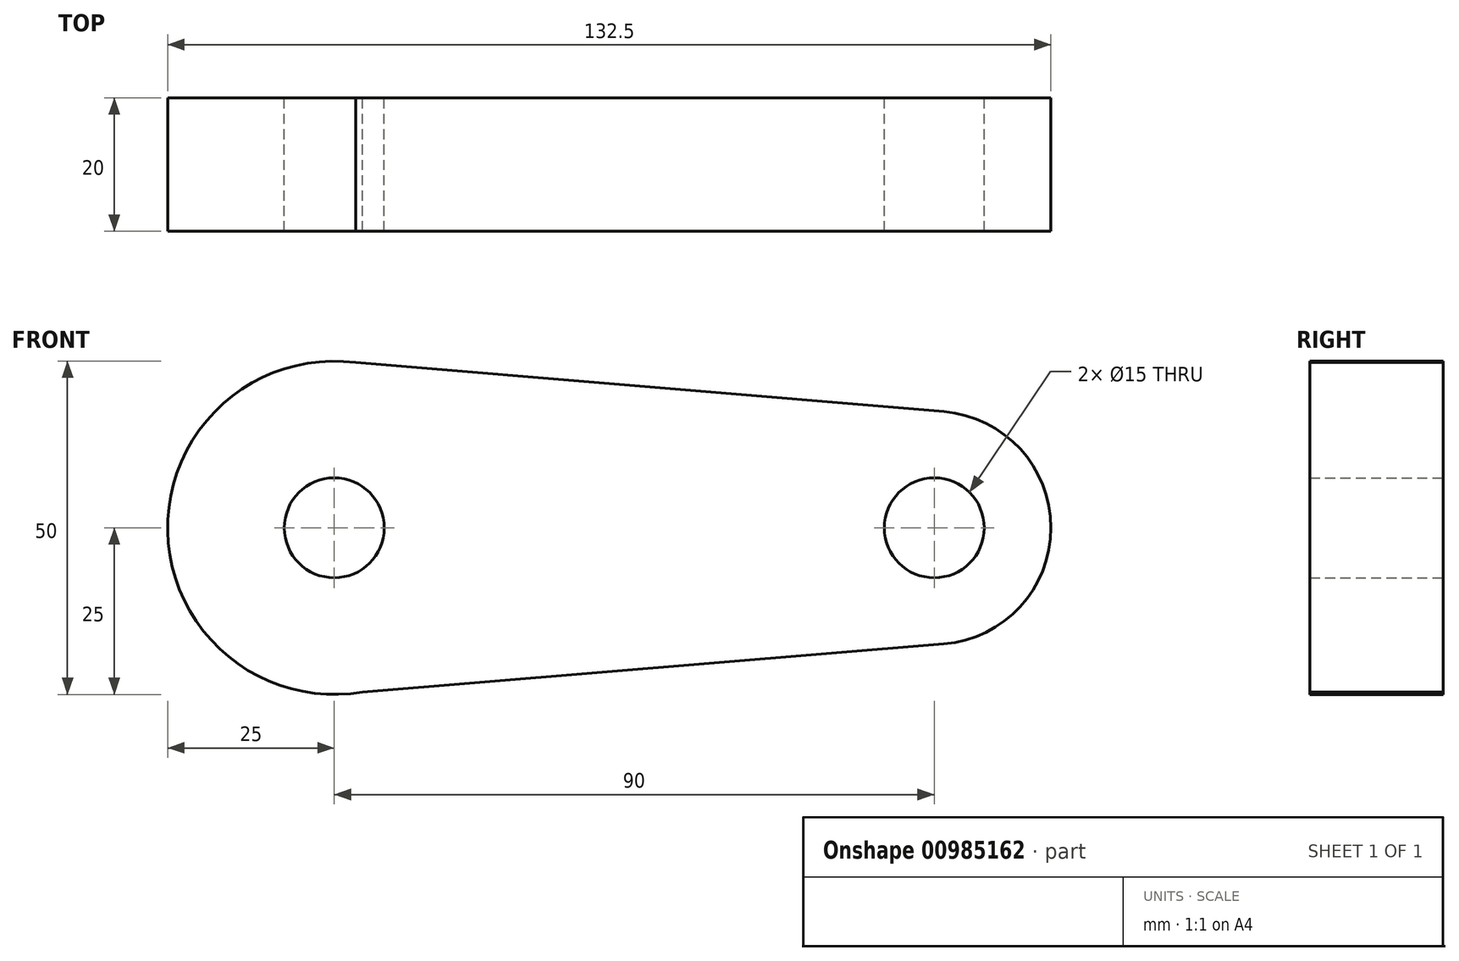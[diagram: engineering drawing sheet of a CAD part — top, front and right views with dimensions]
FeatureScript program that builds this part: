
annotation { "Feature Type Name" : "Feature", "Feature Type Description" : "" }
export const myFeature = defineFeature(function(context is Context, id is Id, definition is map)
    precondition{}
    {
        {
            var Q0;
            Q0=qCreatedBy(makeId("Front.planeOp"),FACE);
            var sketch = newSketch(context, id + "F0", { "sketchPlane" : qUnion([Q0])});
            skCircle(sketch, "E0", {"center": v(0, 0) * mm, "radius": 25 * mm});
            skCircle(sketch, "E1", {"center": v(90, 0) * mm, "radius": 17.5 * mm});
            skLineSegment(sketch, "E2", {"start": v(-0.15, -25) * mm, "end": v(91.44, -17.44) * mm});
            skLineSegment(sketch, "E3", {"start": v(0.95, 24.98) * mm, "end": v(91.45, 17.44) * mm});
            skCircle(sketch, "E4", {"center": v(0, 0) * mm, "radius": 7.5 * mm});
            skCircle(sketch, "E5", {"center": v(90, 0) * mm, "radius": 7.5 * mm});
            skSolve(sketch);
        }
        {
            var Q0;
            Q0 = qSketchRegion(id + "F0", true);
            extrude(context, id + "F1", {"entities" : qUnion([Q0]), "depth" : 20 * mm, "offsetDistance" : 25 * mm});
        }
    });
